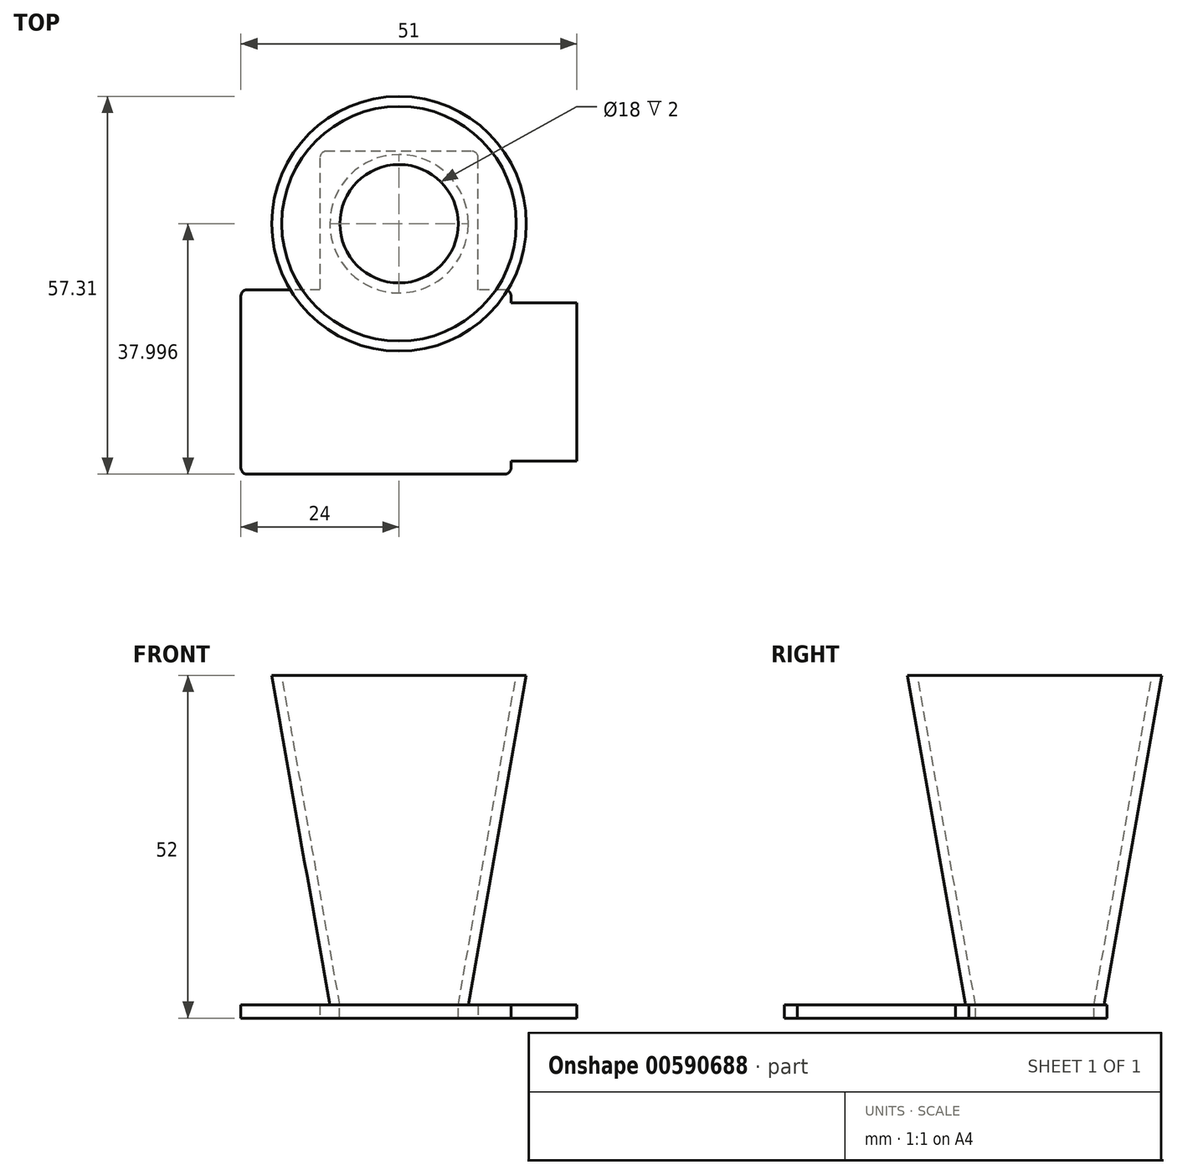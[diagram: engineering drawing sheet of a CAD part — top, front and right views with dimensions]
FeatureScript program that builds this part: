
annotation { "Feature Type Name" : "Feature", "Feature Type Description" : "" }
export const myFeature = defineFeature(function(context is Context, id is Id, definition is map)
    precondition{}
    {
        {
            var Q0;
            Q0=qCreatedBy(makeId("Top.planeOp"),FACE);
            var sketch = newSketch(context, id + "F0", { "sketchPlane" : qUnion([Q0])});
            skLineSegment(sketch, "E0", {"start": v(-24, 8.72) * mm, "end": v(-24, -19.28) * mm});
            skLineSegment(sketch, "E1", {"start": v(-24, -19.28) * mm, "end": v(17, -19.28) * mm});
            skLineSegment(sketch, "E2", {"start": v(17, -19.28) * mm, "end": v(17, 8.72) * mm});
            skLineSegment(sketch, "E3", {"start": v(17, 8.72) * mm, "end": v(12, 8.72) * mm});
            skLineSegment(sketch, "E4", {"start": v(12, 8.72) * mm, "end": v(12, 29.72) * mm});
            skLineSegment(sketch, "E5", {"start": v(12, 29.72) * mm, "end": v(-12, 29.72) * mm});
            skLineSegment(sketch, "E6", {"start": v(-12, 29.72) * mm, "end": v(-12, 8.72) * mm});
            skLineSegment(sketch, "E7", {"start": v(-12, 8.72) * mm, "end": v(-24, 8.72) * mm});
            skSolve(sketch);
        }
        {
            var Q0;
            Q0 = qSketchRegion(id + "F0", true);
            extrude(context, id + "F1", {"entities" : qUnion([Q0]), "depth" : 2 * mm, "offsetDistance" : 25 * mm});
        }
        {
            var Q0;
            Q0=makeQuery(id+"F1.opExtrude","SWEPT_EDGE",EDGE,{"disambiguationData":[OSD([sQuery(id+"F0.wireOp",EDGE,"E0"),sQuery(id+"F0.wireOp",EDGE,"E7")])]});
            var Q1;
            Q1=makeQuery(id+"F1.opExtrude","SWEPT_EDGE",EDGE,{"disambiguationData":[OSD([sQuery(id+"F0.wireOp",EDGE,"E5"),sQuery(id+"F0.wireOp",EDGE,"E6")])]});
            var Q2;
            Q2=makeQuery(id+"F1.opExtrude","SWEPT_EDGE",EDGE,{"disambiguationData":[OSD([sQuery(id+"F0.wireOp",EDGE,"E4"),sQuery(id+"F0.wireOp",EDGE,"E5")])]});
            var Q3;
            Q3=makeQuery(id+"F1.opExtrude","SWEPT_EDGE",EDGE,{"disambiguationData":[OSD([sQuery(id+"F0.wireOp",EDGE,"E2"),sQuery(id+"F0.wireOp",EDGE,"E3")])]});
            var Q4;
            Q4=makeQuery(id+"F1.opExtrude","SWEPT_EDGE",EDGE,{"disambiguationData":[OSD([sQuery(id+"F0.wireOp",EDGE,"E1"),sQuery(id+"F0.wireOp",EDGE,"E2")])]});
            var Q5;
            Q5=makeQuery(id+"F1.opExtrude","SWEPT_EDGE",EDGE,{"disambiguationData":[OSD([sQuery(id+"F0.wireOp",EDGE,"E0"),sQuery(id+"F0.wireOp",EDGE,"E1")])]});
            fillet(context, id + "F2", {"entities" : qUnion([Q0, Q1, Q2, Q3, Q4, Q5]), "radius" : 1 * mm, "tangentPropagation" : true, "allowEdgeOverflow" : false});
        }
        {
            var Q0;
            Q0=makeQuery(id+"F1.opExtrude","CAP_FACE",FACE,{"disambiguationData":[OSD([sQuery(id+"F0.wireOp",EDGE,"E0"),sQuery(id+"F0.wireOp",EDGE,"E1"),sQuery(id+"F0.wireOp",EDGE,"E2"),sQuery(id+"F0.wireOp",EDGE,"E3"),sQuery(id+"F0.wireOp",EDGE,"E4"),sQuery(id+"F0.wireOp",EDGE,"E5"),sQuery(id+"F0.wireOp",EDGE,"E6"),sQuery(id+"F0.wireOp",EDGE,"E7")])],"isStart":false});
            var sketch = newSketch(context, id + "F3", { "sketchPlane" : qUnion([Q0])});
            skCircle(sketch, "E8", {"center": v(0, 18.72) * mm, "radius": 9 * mm});
            skSolve(sketch);
        }
        {
            var Q0;
            Q0 = qSketchRegion(id + "F3", true);
            extrude(context, id + "F4", {"entities" : qUnion([Q0]), "operationType" : NewBodyOperationType.REMOVE, "endBound" : BoundingType.UP_TO_NEXT, "oppositeDirection" : true, "depth" : 25 * mm, "offsetDistance" : 25 * mm});
        }
        {
            var Q0;
            Q0=qCreatedBy(makeId("Right.planeOp"),FACE);
            var sketch = newSketch(context, id + "F5", { "sketchPlane" : qUnion([Q0])});
            skLineSegment(sketch, "E9", {"start": v(27.7, 2) * mm, "end": v(36.5, 52) * mm});
            skLineSegment(sketch, "E10", {"start": v(36.5, 52) * mm, "end": v(38.03, 52) * mm});
            skLineSegment(sketch, "E11", {"start": v(38.03, 52) * mm, "end": v(29.22, 2) * mm});
            skLineSegment(sketch, "E12", {"start": v(29.22, 2) * mm, "end": v(27.7, 2) * mm});
            skSolve(sketch);
        }
        {
            var Q0;
            Q0=qCreatedBy(makeId("Right.planeOp"),FACE);
            var sketch = newSketch(context, id + "F6", { "sketchPlane" : qUnion([Q0])});
            skLineSegment(sketch, "E13", {"start": v(18.72, 2) * mm, "end": v(18.72, 19.03) * mm, "construction": true});
            skSolve(sketch);
        }
        {
            var Q0;
            Q0 = qSketchRegion(id + "F5", true);
            var Q1;
            Q1=sQuery(id+"F6.wireOp",EDGE,"E13");
            revolve(context, id + "F7", {"operationType" : NewBodyOperationType.ADD, "entities" : qUnion([Q0]), "axis" : qUnion([Q1]), "revolveType" : RevolveType.FULL});
        }
        {
            var Q0;
            Q0=makeQuery(id+"F1.opExtrude","SWEPT_FACE",FACE,{"disambiguationData":[OSD([sQuery(id+"F0.wireOp",EDGE,"E2")])]});
            var sketch = newSketch(context, id + "F8", { "sketchPlane" : qUnion([Q0])});
            skLineSegment(sketch, "E14.bottom", {"start": v(-17.28, 2) * mm, "end": v(6.72, 2) * mm});
            skLineSegment(sketch, "E14.top", {"start": v(-17.28, 0) * mm, "end": v(6.72, 0) * mm});
            skLineSegment(sketch, "E14.left", {"start": v(-17.28, 2) * mm, "end": v(-17.28, 0) * mm});
            skLineSegment(sketch, "E14.right", {"start": v(6.72, 2) * mm, "end": v(6.72, 0) * mm});
            skSolve(sketch);
        }
        {
            var Q0;
            Q0 = qSketchRegion(id + "F8", true);
            extrude(context, id + "F9", {"entities" : qUnion([Q0]), "operationType" : NewBodyOperationType.ADD, "depth" : 10 * mm, "offsetDistance" : 25 * mm});
        }
    });
